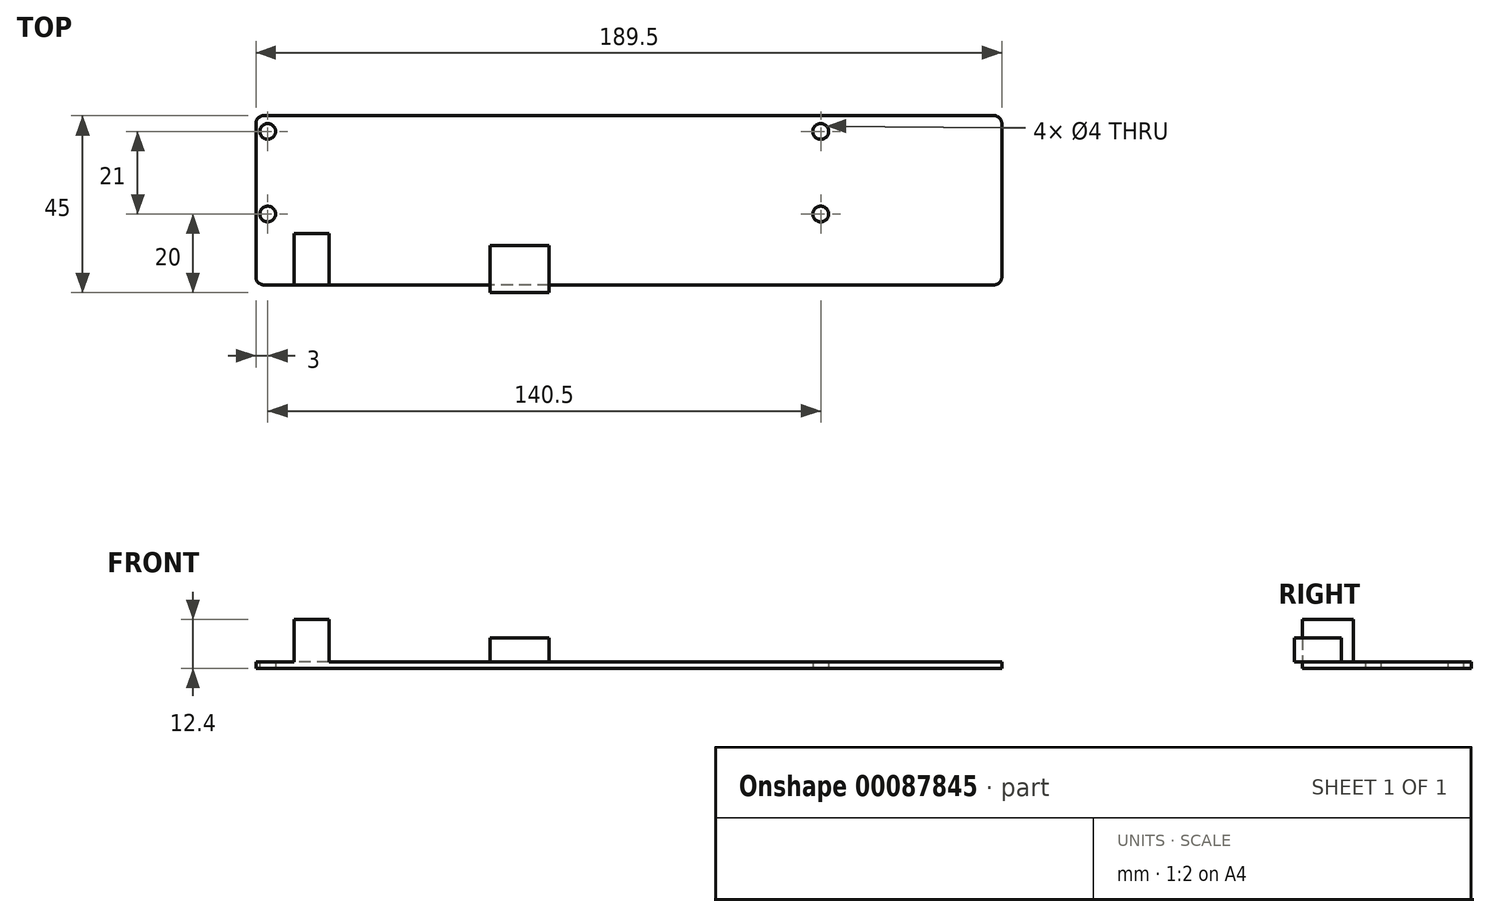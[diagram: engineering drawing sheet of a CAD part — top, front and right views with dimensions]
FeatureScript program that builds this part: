
annotation { "Feature Type Name" : "Feature", "Feature Type Description" : "" }
export const myFeature = defineFeature(function(context is Context, id is Id, definition is map)
    precondition{}
    {
        {
            var Q0;
            Q0=qCreatedBy(makeId("Top.planeOp"),FACE);
            var sketch = newSketch(context, id + "F0", { "sketchPlane" : qUnion([Q0])});
            skLineSegment(sketch, "E0.bottom", {"start": v(92.75, -21.5) * mm, "end": v(-92.75, -21.5) * mm});
            skLineSegment(sketch, "E0.top", {"start": v(92.75, 21.5) * mm, "end": v(-92.75, 21.5) * mm});
            skLineSegment(sketch, "E0.left", {"start": v(94.75, -19.5) * mm, "end": v(94.75, 19.5) * mm});
            skLineSegment(sketch, "E0.right", {"start": v(-94.75, -19.5) * mm, "end": v(-94.75, 19.5) * mm});
            skPoint(sketch, "E0.middle", {"position": v(0, 0) * mm});
            skCircle(sketch, "E1", {"center": v(-91.75, -3.5) * mm, "radius": 2 * mm});
            skCircle(sketch, "E2", {"center": v(-91.75, 17.5) * mm, "radius": 2 * mm});
            skCircle(sketch, "E3", {"center": v(48.75, -3.5) * mm, "radius": 2 * mm});
            skCircle(sketch, "E4", {"center": v(48.75, 17.5) * mm, "radius": 2 * mm});
            skPoint(sketch, "E5.visualSharp", {"position": v(-94.75, 21.5) * mm});
            skArc(sketch, "E5.filletArc", {"start": v(-92.75, 21.5) * mm, "mid": v(-94.16, 20.91) * mm, "end": v(-94.75, 19.5) * mm});
            skPoint(sketch, "E6.visualSharp", {"position": v(-94.75, -21.5) * mm});
            skArc(sketch, "E6.filletArc", {"start": v(-94.75, -19.5) * mm, "mid": v(-94.16, -20.91) * mm, "end": v(-92.75, -21.5) * mm});
            skPoint(sketch, "E7.visualSharp", {"position": v(94.75, -21.5) * mm});
            skArc(sketch, "E7.filletArc", {"start": v(92.75, -21.5) * mm, "mid": v(94.16, -20.91) * mm, "end": v(94.75, -19.5) * mm});
            skPoint(sketch, "E8.visualSharp", {"position": v(94.75, 21.5) * mm});
            skArc(sketch, "E8.filletArc", {"start": v(94.75, 19.5) * mm, "mid": v(94.16, 20.91) * mm, "end": v(92.75, 21.5) * mm});
            skSolve(sketch);
        }
        {
            var Q0;
            Q0=makeQuery(id+"F0.imprint","IMPRINT",FACE,{"disambiguationData":[TD([[makeQuery(id+"F0.imprint","IMPRINT",EDGE,{"derivedFrom":sQuery(id+"F0.wireOp",EDGE,"E0.bottom")}),-1.0]])]});
            extrude(context, id + "F1", {"entities" : qUnion([Q0]), "depth" : 1.6 * mm});
        }
        {
            var Q0;
            Q0=makeQuery(id+"F1.opExtrude","CAP_FACE",FACE,{"disambiguationData":[OSD([sQuery(id+"F0.wireOp",EDGE,"E0.bottom"),sQuery(id+"F0.wireOp",EDGE,"E0.top"),sQuery(id+"F0.wireOp",EDGE,"E0.left"),sQuery(id+"F0.wireOp",EDGE,"E0.right"),sQuery(id+"F0.wireOp",EDGE,"E1"),sQuery(id+"F0.wireOp",EDGE,"E2"),sQuery(id+"F0.wireOp",EDGE,"E3"),sQuery(id+"F0.wireOp",EDGE,"E4"),sQuery(id+"F0.wireOp",EDGE,"E5.filletArc"),sQuery(id+"F0.wireOp",EDGE,"E6.filletArc"),sQuery(id+"F0.wireOp",EDGE,"E7.filletArc"),sQuery(id+"F0.wireOp",EDGE,"E8.filletArc")])],"isStart":false});
            var sketch = newSketch(context, id + "F2", { "sketchPlane" : qUnion([Q0])});
            skLineSegment(sketch, "E9.bottom", {"start": v(-76.2, -21.5) * mm, "end": v(-85.1, -21.5) * mm});
            skLineSegment(sketch, "E9.top", {"start": v(-76.2, -8.5) * mm, "end": v(-85.1, -8.5) * mm});
            skLineSegment(sketch, "E9.left", {"start": v(-76.2, -21.5) * mm, "end": v(-76.2, -8.5) * mm});
            skLineSegment(sketch, "E9.right", {"start": v(-85.1, -21.5) * mm, "end": v(-85.1, -8.5) * mm});
            skPoint(sketch, "E9.middle", {"position": v(-80.65, -15) * mm});
            skSolve(sketch);
        }
        {
            var Q0;
            Q0 = qSketchRegion(id + "F2", true);
            extrude(context, id + "F3", {"entities" : qUnion([Q0]), "operationType" : NewBodyOperationType.ADD, "depth" : 10.8 * mm});
        }
        {
            var Q0;
            Q0=makeQuery(id+"F1.opExtrude","CAP_FACE",FACE,{"disambiguationData":[OSD([sQuery(id+"F0.wireOp",EDGE,"E0.bottom"),sQuery(id+"F0.wireOp",EDGE,"E0.top"),sQuery(id+"F0.wireOp",EDGE,"E0.left"),sQuery(id+"F0.wireOp",EDGE,"E0.right"),sQuery(id+"F0.wireOp",EDGE,"E1"),sQuery(id+"F0.wireOp",EDGE,"E2"),sQuery(id+"F0.wireOp",EDGE,"E3"),sQuery(id+"F0.wireOp",EDGE,"E4"),sQuery(id+"F0.wireOp",EDGE,"E5.filletArc"),sQuery(id+"F0.wireOp",EDGE,"E6.filletArc"),sQuery(id+"F0.wireOp",EDGE,"E7.filletArc"),sQuery(id+"F0.wireOp",EDGE,"E8.filletArc")])],"isStart":false});
            var sketch = newSketch(context, id + "F4", { "sketchPlane" : qUnion([Q0])});
            skLineSegment(sketch, "E10.bottom", {"start": v(-20.25, -23.5) * mm, "end": v(-35.25, -23.5) * mm});
            skLineSegment(sketch, "E10.top", {"start": v(-20.25, -11.5) * mm, "end": v(-35.25, -11.5) * mm});
            skLineSegment(sketch, "E10.left", {"start": v(-20.25, -23.5) * mm, "end": v(-20.25, -11.5) * mm});
            skLineSegment(sketch, "E10.right", {"start": v(-35.25, -23.5) * mm, "end": v(-35.25, -11.5) * mm});
            skPoint(sketch, "E10.middle", {"position": v(-27.75, -17.5) * mm});
            skSolve(sketch);
        }
        {
            var Q0;
            Q0 = qSketchRegion(id + "F4", true);
            extrude(context, id + "F5", {"entities" : qUnion([Q0]), "operationType" : NewBodyOperationType.ADD, "depth" : 6.1 * mm});
        }
    });
